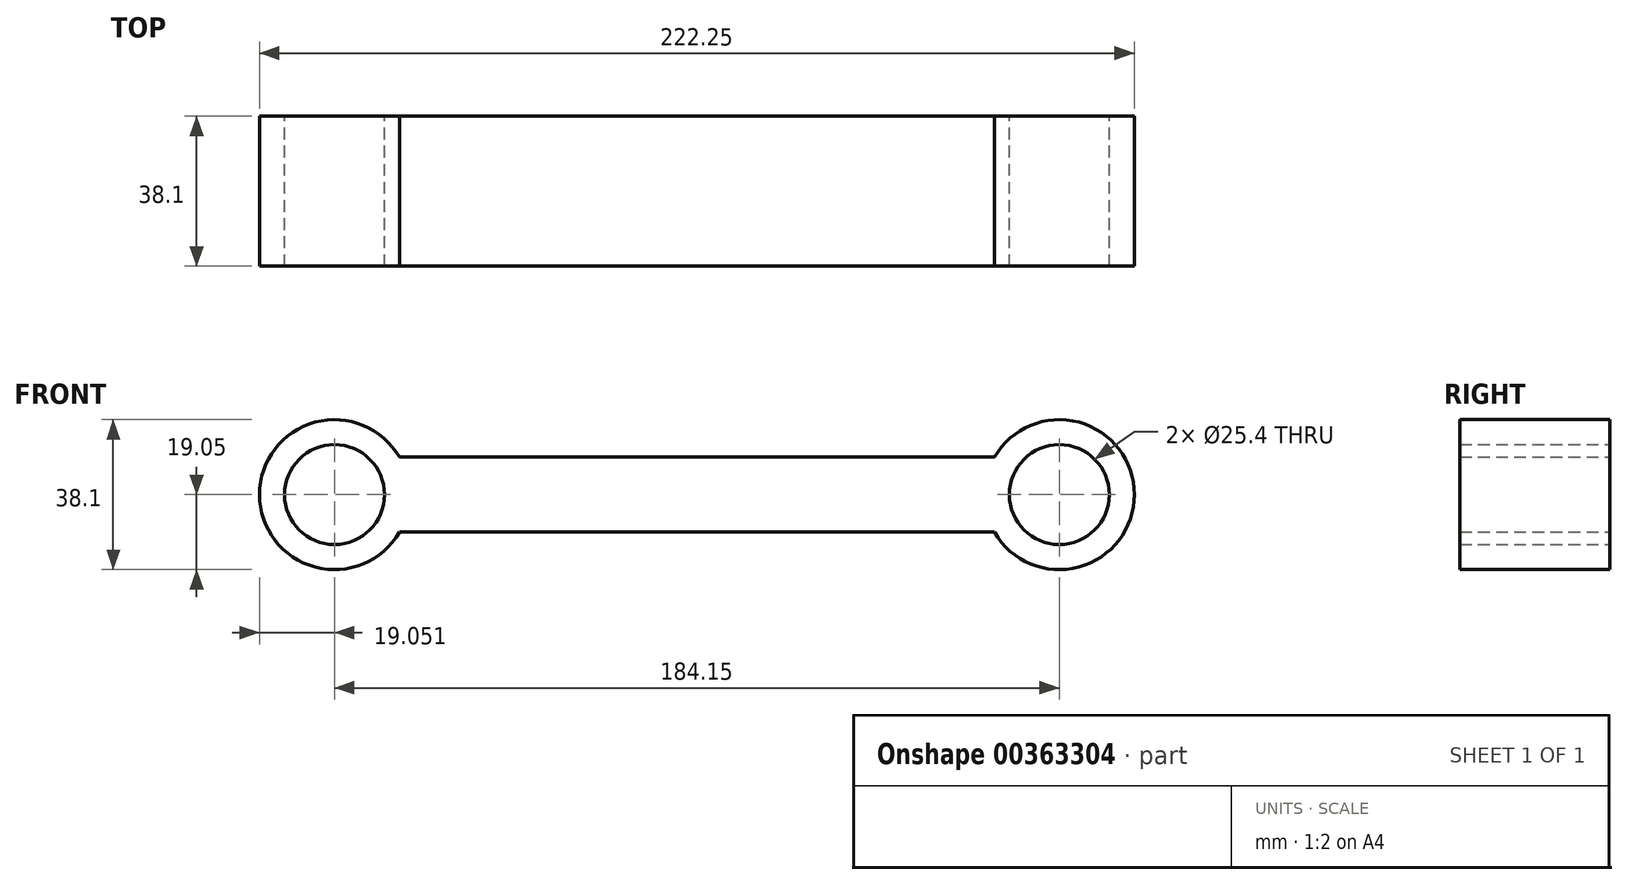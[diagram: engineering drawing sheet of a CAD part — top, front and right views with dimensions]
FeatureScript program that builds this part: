
annotation { "Feature Type Name" : "Feature", "Feature Type Description" : "" }
export const myFeature = defineFeature(function(context is Context, id is Id, definition is map)
    precondition{}
    {
        {
            var Q0;
            Q0=qCreatedBy(makeId("Front.planeOp"),FACE);
            var sketch = newSketch(context, id + "F0", { "sketchPlane" : qUnion([Q0])});
            skCircle(sketch, "E0", {"center": v(-61.8, 0) * mm, "radius": 19.05 * mm});
            skCircle(sketch, "E1", {"center": v(-61.8, 0) * mm, "radius": 12.7 * mm});
            skLineSegment(sketch, "E2.bottom", {"start": v(-45.3, 9.52) * mm, "end": v(107.1, 9.52) * mm});
            skLineSegment(sketch, "E2.top", {"start": v(-45.3, -9.52) * mm, "end": v(107.1, -9.52) * mm});
            skLineSegment(sketch, "E2.left", {"start": v(-45.3, 9.52) * mm, "end": v(-45.3, -9.52) * mm});
            skLineSegment(sketch, "E2.right", {"start": v(107.1, 9.52) * mm, "end": v(107.1, -9.52) * mm});
            skCircle(sketch, "E3", {"center": v(122.35, 0) * mm, "radius": 19.05 * mm});
            skCircle(sketch, "E4", {"center": v(122.35, 0) * mm, "radius": 12.7 * mm});
            skLineSegment(sketch, "E5.bottom", {"start": v(105.85, -9.52) * mm, "end": v(-46.55, -9.53) * mm});
            skLineSegment(sketch, "E5.top", {"start": v(105.85, 9.53) * mm, "end": v(-46.55, 9.53) * mm});
            skLineSegment(sketch, "E5.left", {"start": v(105.85, -9.53) * mm, "end": v(105.85, 9.53) * mm});
            skLineSegment(sketch, "E5.right", {"start": v(-46.55, -9.53) * mm, "end": v(-46.55, 9.53) * mm});
            skSolve(sketch);
        }
        {
            var Q0;
            Q0 = qSketchRegion(id + "F0", true);
            extrude(context, id + "F1", {"entities" : qUnion([Q0]), "depth" : 38.1 * mm});
        }
    });
